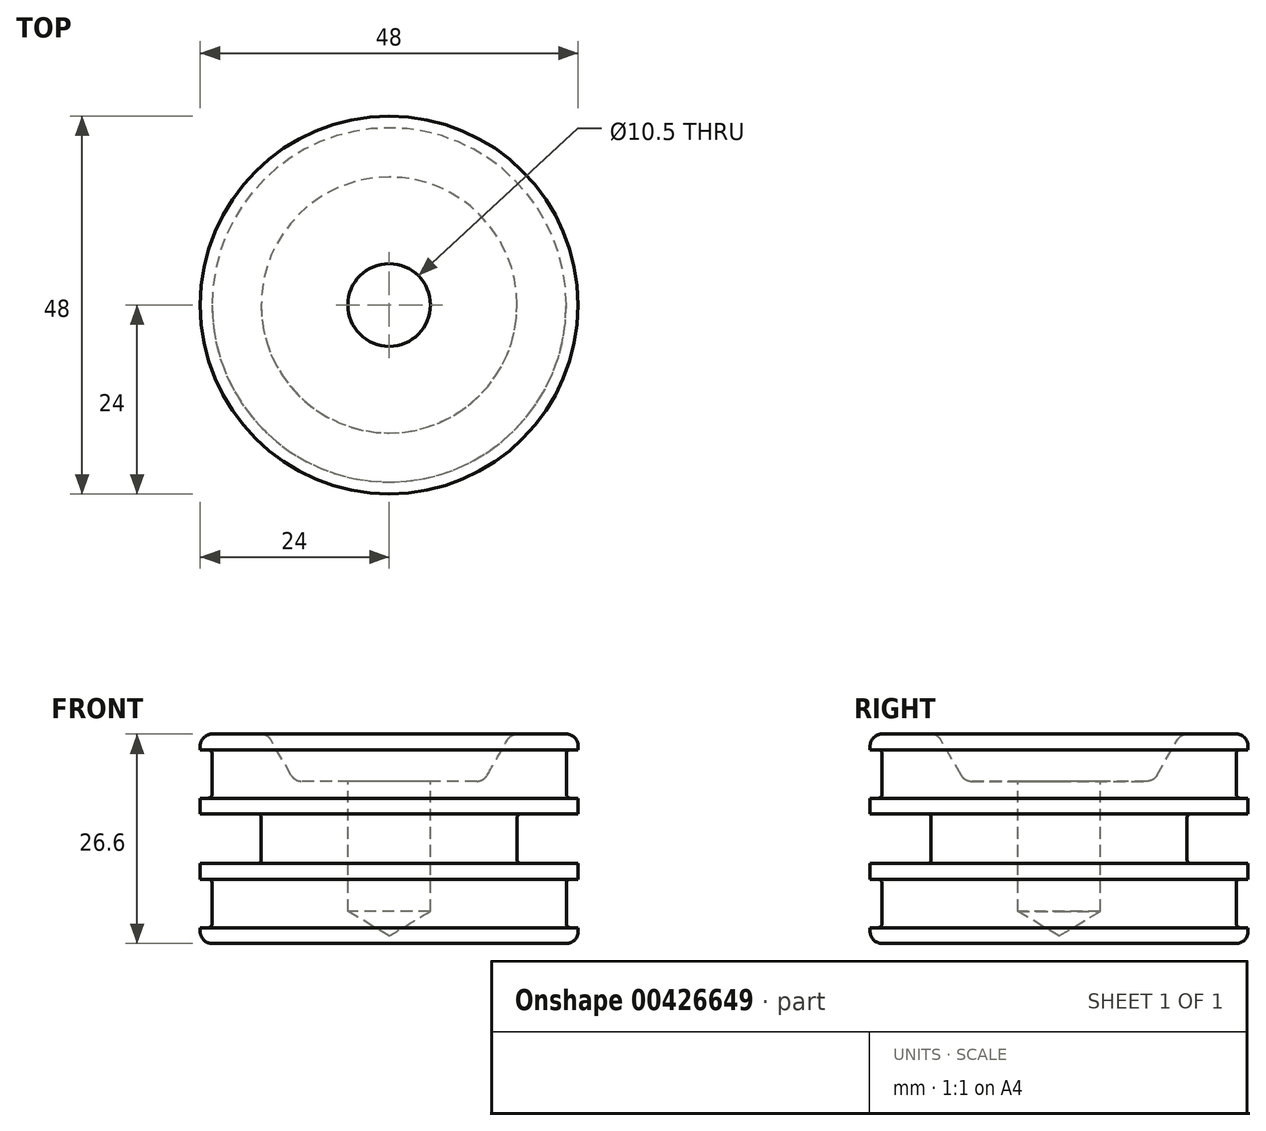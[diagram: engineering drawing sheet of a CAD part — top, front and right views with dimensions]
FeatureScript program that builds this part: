
annotation { "Feature Type Name" : "Feature", "Feature Type Description" : "" }
export const myFeature = defineFeature(function(context is Context, id is Id, definition is map)
    precondition{}
    {
        {
            var Q0;
            Q0=qCreatedBy(makeId("Front.planeOp"),FACE);
            var sketch = newSketch(context, id + "F0", { "sketchPlane" : qUnion([Q0])});
            skLineSegment(sketch, "E0", {"start": v(15.46, 13.3) * mm, "end": v(24, 13.3) * mm});
            skLineSegment(sketch, "E1", {"start": v(24, 13.3) * mm, "end": v(24, 11.3) * mm});
            skLineSegment(sketch, "E2", {"start": v(24, 11.3) * mm, "end": v(22.5, 11.3) * mm});
            skLineSegment(sketch, "E3", {"start": v(22.5, 11.3) * mm, "end": v(22.5, 5.15) * mm});
            skLineSegment(sketch, "E4", {"start": v(22.5, 5.15) * mm, "end": v(24, 5.15) * mm});
            skLineSegment(sketch, "E5", {"start": v(24, 5.15) * mm, "end": v(24, 3.15) * mm});
            skLineSegment(sketch, "E6", {"start": v(24, -3.15) * mm, "end": v(24, -5.15) * mm});
            skLineSegment(sketch, "E7", {"start": v(24, -5.15) * mm, "end": v(22.5, -5.15) * mm});
            skLineSegment(sketch, "E8", {"start": v(22.5, -5.15) * mm, "end": v(22.5, -11.3) * mm});
            skLineSegment(sketch, "E9", {"start": v(22.5, -11.3) * mm, "end": v(24, -11.3) * mm});
            skLineSegment(sketch, "E10", {"start": v(24, -11.3) * mm, "end": v(24, -13.3) * mm});
            skLineSegment(sketch, "E11", {"start": v(24, -13.3) * mm, "end": v(0, -13.3) * mm});
            skLineSegment(sketch, "E12", {"start": v(0, -13.3) * mm, "end": v(0, 7.3) * mm});
            skLineSegment(sketch, "E13", {"start": v(24, 3.15) * mm, "end": v(16.25, 3.15) * mm});
            skLineSegment(sketch, "E14", {"start": v(16.25, 3.15) * mm, "end": v(16.25, -3.15) * mm});
            skLineSegment(sketch, "E15", {"start": v(16.25, -3.15) * mm, "end": v(24, -3.15) * mm});
            skLineSegment(sketch, "E16", {"start": v(15.46, 13.3) * mm, "end": v(12, 7.3) * mm});
            skLineSegment(sketch, "E17", {"start": v(12, 7.3) * mm, "end": v(0, 7.3) * mm});
            skPoint(sketch, "E18.orphan", {"position": v(0, 13.3) * mm});
            skLineSegment(sketch, "E19", {"start": v(16.25, 0) * mm, "end": v(0, 0) * mm, "construction": true});
            skSolve(sketch);
        }
        {
            var Q0;
            Q0=makeQuery(id+"F0.imprint","IMPRINT",FACE,{"disambiguationData":[TD([[makeQuery(id+"F0.imprint","IMPRINT",EDGE,{"derivedFrom":sQuery(id+"F0.wireOp",EDGE,"E0")}),-1.0]])]});
            var Q1;
            Q1=sQuery(id+"F0.wireOp",EDGE,"E12");
            revolve(context, id + "F1", {"surfaceOperationType" : NewSurfaceOperationType.NEW, "entities" : qUnion([Q0]), "axis" : qUnion([Q1]), "revolveType" : RevolveType.FULL});
        }
        {
            var Q0;
            Q0=makeQuery(id+"F1.opRevolve","SWEPT_EDGE",EDGE,{"disambiguationData":[OSD([sQuery(id+"F0.wireOp",EDGE,"E14"),sQuery(id+"F0.wireOp",EDGE,"E15")])]});
            var Q1;
            Q1=makeQuery(id+"F1.opRevolve","SWEPT_EDGE",EDGE,{"disambiguationData":[OSD([sQuery(id+"F0.wireOp",EDGE,"E13"),sQuery(id+"F0.wireOp",EDGE,"E14")])]});
            var Q2;
            Q2=makeQuery(id+"F1.opRevolve","SWEPT_EDGE",EDGE,{"disambiguationData":[OSD([sQuery(id+"F0.wireOp",EDGE,"E2"),sQuery(id+"F0.wireOp",EDGE,"E3")])]});
            var Q3;
            Q3=makeQuery(id+"F1.opRevolve","SWEPT_EDGE",EDGE,{"disambiguationData":[OSD([sQuery(id+"F0.wireOp",EDGE,"E3"),sQuery(id+"F0.wireOp",EDGE,"E4")])]});
            var Q4;
            Q4=makeQuery(id+"F1.opRevolve","SWEPT_EDGE",EDGE,{"disambiguationData":[OSD([sQuery(id+"F0.wireOp",EDGE,"E8"),sQuery(id+"F0.wireOp",EDGE,"E9")])]});
            var Q5;
            Q5=makeQuery(id+"F1.opRevolve","SWEPT_EDGE",EDGE,{"disambiguationData":[OSD([sQuery(id+"F0.wireOp",EDGE,"E7"),sQuery(id+"F0.wireOp",EDGE,"E8")])]});
            fillet(context, id + "F2", {"entities" : qUnion([Q0, Q1, Q2, Q3, Q4, Q5]), "radius" : .5 * mm, "tangentPropagation" : true, "allowEdgeOverflow" : false});
        }
        {
            var Q0;
            Q0=makeQuery(id+"F1.opRevolve","SWEPT_EDGE",EDGE,{"disambiguationData":[OSD([sQuery(id+"F0.wireOp",EDGE,"E0"),sQuery(id+"F0.wireOp",EDGE,"E1")])]});
            var Q1;
            Q1=makeQuery(id+"F1.opRevolve","SWEPT_EDGE",EDGE,{"disambiguationData":[OSD([sQuery(id+"F0.wireOp",EDGE,"E10"),sQuery(id+"F0.wireOp",EDGE,"E11")])]});
            var Q2;
            Q2=makeQuery(id+"F1.opRevolve","SWEPT_EDGE",EDGE,{"disambiguationData":[OSD([sQuery(id+"F0.wireOp",EDGE,"E16"),sQuery(id+"F0.wireOp",EDGE,"E17")])]});
            var Q3;
            Q3=makeQuery(id+"F1.opRevolve","SWEPT_EDGE",EDGE,{"disambiguationData":[OSD([sQuery(id+"F0.wireOp",EDGE,"E0"),sQuery(id+"F0.wireOp",EDGE,"E16")])]});
            fillet(context, id + "F3", {"entities" : qUnion([Q0, Q1, Q2, Q3]), "radius" : 1.5 * mm, "tangentPropagation" : true, "allowEdgeOverflow" : false});
        }
        {
            var Q0;
            Q0=makeQuery(id+"F1.opRevolve","SWEPT_FACE",FACE,{"disambiguationData":[OSD([sQuery(id+"F0.wireOp",EDGE,"E17")])]});
            var sketch = newSketch(context, id + "F4", { "sketchPlane" : qUnion([Q0])});
            skPoint(sketch, "E20", {"position": v(0, 0) * mm});
            skSolve(sketch);
        }
        {
            var Q0;
            Q0=sQuery(id+"F4.wireOp",VERTEX,"E20");
            var Q1;
            Q1=makeQuery(id+"F1.opRevolve","SWEPT_BODY",BODY,{"disambiguationData":[OSD([sQuery(id+"F0.wireOp",EDGE,"E0"),sQuery(id+"F0.wireOp",EDGE,"E1"),sQuery(id+"F0.wireOp",EDGE,"E2"),sQuery(id+"F0.wireOp",EDGE,"E3"),sQuery(id+"F0.wireOp",EDGE,"E4"),sQuery(id+"F0.wireOp",EDGE,"E5"),sQuery(id+"F0.wireOp",EDGE,"E6"),sQuery(id+"F0.wireOp",EDGE,"E7"),sQuery(id+"F0.wireOp",EDGE,"E8"),sQuery(id+"F0.wireOp",EDGE,"E9"),sQuery(id+"F0.wireOp",EDGE,"E10"),sQuery(id+"F0.wireOp",EDGE,"E11"),sQuery(id+"F0.wireOp",EDGE,"E12"),sQuery(id+"F0.wireOp",EDGE,"E13"),sQuery(id+"F0.wireOp",EDGE,"E14"),sQuery(id+"F0.wireOp",EDGE,"E15"),sQuery(id+"F0.wireOp",EDGE,"E16"),sQuery(id+"F0.wireOp",EDGE,"E17")])]});
            hole(context, id + "F5", {"style" : HoleStyle.SIMPLE, "endStyle" : HoleEndStyle.BLIND, "standardTappedOrClearance" : lookupTablePath({ "standard" : "ISO", "engagement" : "75%", "pitch" : "1.5 mm", "size" : "M12", "type" : "Tapped" }), "standardBlindInLast" : lookupTablePath({ "standard" : "ISO", "engagement" : "75%", "pitch" : "1.5 mm", "size" : "M12", "type" : "Tapped" }), "holeDiameter" : 10.5 * mm, "majorDiameter" : 12 * mm, "showTappedDepth" : true, "holeDepth" : 16.5 * mm, "isTappedThrough" : true, "tappedDepth" : 12 * mm, "tapClearance" : 3, "locations" : qUnion([Q0]), "scope" : qUnion([Q1])});
        }
    });
